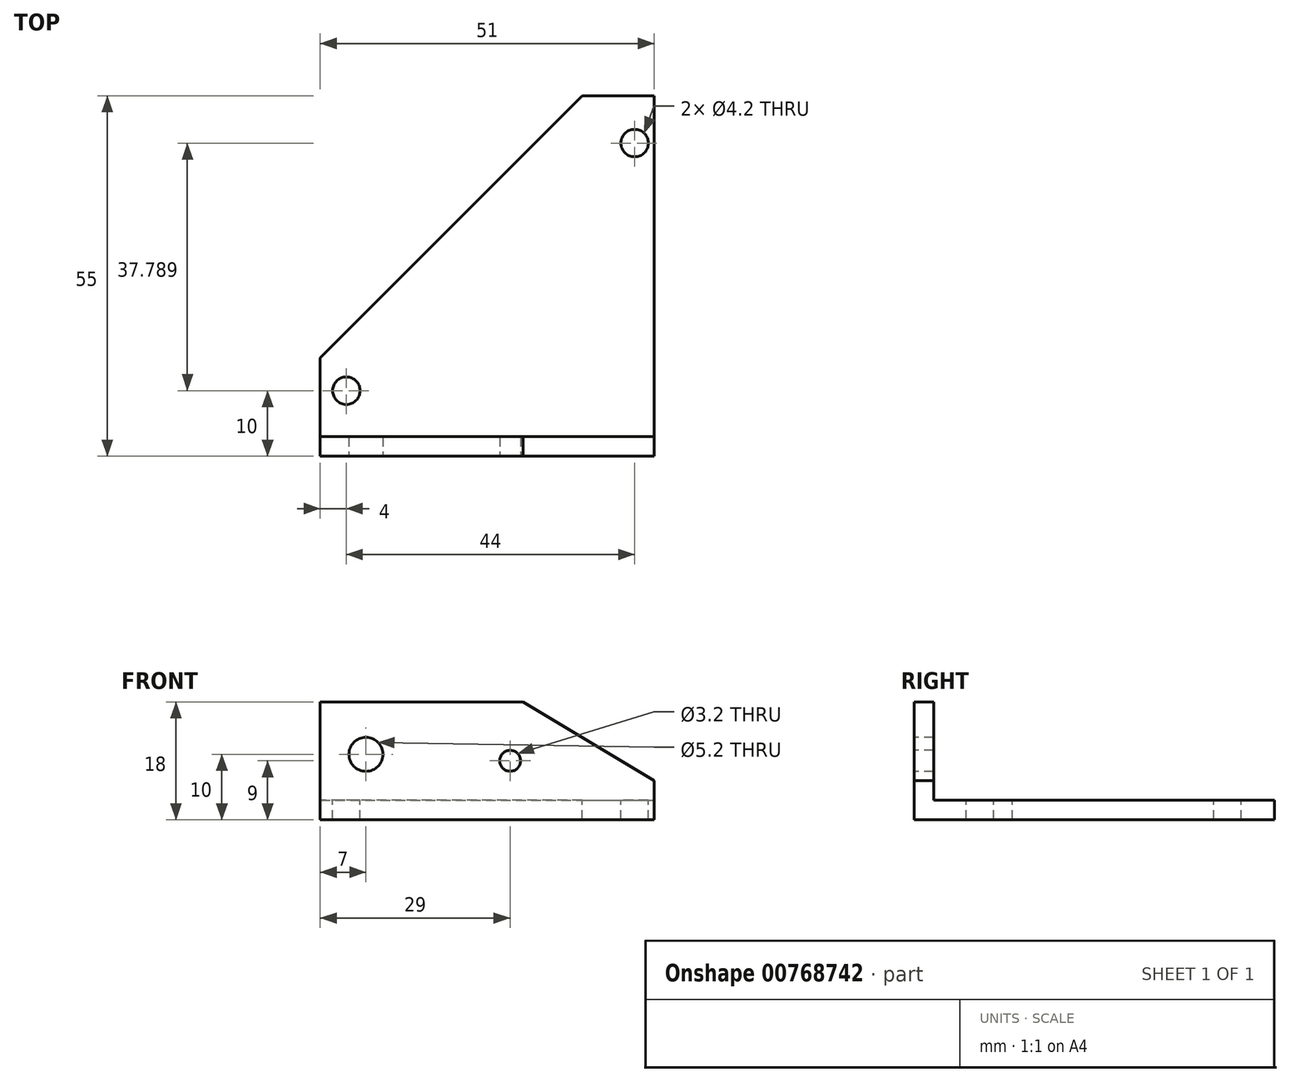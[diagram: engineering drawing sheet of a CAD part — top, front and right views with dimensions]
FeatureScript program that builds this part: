
annotation { "Feature Type Name" : "Feature", "Feature Type Description" : "" }
export const myFeature = defineFeature(function(context is Context, id is Id, definition is map)
    precondition{}
    {
        {
            var Q0;
            Q0=qCreatedBy(makeId("Top.planeOp"),FACE);
            var sketch = newSketch(context, id + "F0", { "sketchPlane" : qUnion([Q0])});
            skLineSegment(sketch, "E0.bottom", {"start": v(0, 0) * mm, "end": v(51, 0) * mm});
            skLineSegment(sketch, "E0.top", {"start": v(0, 55) * mm, "end": v(51, 55) * mm});
            skLineSegment(sketch, "E0.left", {"start": v(0, 0) * mm, "end": v(0, 55) * mm});
            skLineSegment(sketch, "E0.right", {"start": v(51, 0) * mm, "end": v(51, 55) * mm});
            skSolve(sketch);
        }
        {
            var Q0;
            Q0 = qSketchRegion(id + "F0", true);
            extrude(context, id + "F1", {"entities" : qUnion([Q0]), "depth" : 3 * mm, "offsetDistance" : 25 * mm});
        }
        {
            var Q0;
            Q0=makeQuery(id+"F1.opExtrude","CAP_FACE",FACE,{"disambiguationData":[OSD([sQuery(id+"F0.wireOp",EDGE,"E0.bottom"),sQuery(id+"F0.wireOp",EDGE,"E0.top"),sQuery(id+"F0.wireOp",EDGE,"E0.left"),sQuery(id+"F0.wireOp",EDGE,"E0.right")])],"isStart":false});
            var sketch = newSketch(context, id + "F2", { "sketchPlane" : qUnion([Q0])});
            skLineSegment(sketch, "E1.bottom", {"start": v(0, 0) * mm, "end": v(51, 0) * mm});
            skLineSegment(sketch, "E1.top", {"start": v(0, 3) * mm, "end": v(51, 3) * mm});
            skLineSegment(sketch, "E1.left", {"start": v(0, 0) * mm, "end": v(0, 3) * mm});
            skLineSegment(sketch, "E1.right", {"start": v(51, 0) * mm, "end": v(51, 3) * mm});
            skSolve(sketch);
        }
        {
            var Q0;
            Q0 = qSketchRegion(id + "F2", true);
            extrude(context, id + "F3", {"entities" : qUnion([Q0]), "operationType" : NewBodyOperationType.ADD, "depth" : 15 * mm, "offsetDistance" : 25 * mm});
        }
        {
            var Q0;
            Q0=makeQuery(id+"F3.boolean.opBoolean","MERGE",FACE,{"derivedFrom":[makeQuery(id+"F1.opExtrude","SWEPT_FACE",FACE,{"disambiguationData":[OSD([sQuery(id+"F0.wireOp",EDGE,"E0.bottom")])]}),makeQuery(id+"F3.opExtrude","SWEPT_FACE",FACE,{"disambiguationData":[OSD([sQuery(id+"F2.wireOp",EDGE,"E1.bottom")])]})]});
            var sketch = newSketch(context, id + "F4", { "sketchPlane" : qUnion([Q0])});
            skCircle(sketch, "E2", {"center": v(7, 10) * mm, "radius": 2.6 * mm});
            skCircle(sketch, "E3", {"center": v(29, 9) * mm, "radius": 1.6 * mm});
            skSolve(sketch);
        }
        {
            var Q0;
            Q0 = qSketchRegion(id + "F4", true);
            extrude(context, id + "F5", {"entities" : qUnion([Q0]), "operationType" : NewBodyOperationType.REMOVE, "oppositeDirection" : true, "depth" : 25 * mm, "offsetDistance" : 25 * mm});
        }
        {
            var Q0;
            Q0=makeQuery(id+"F1.opExtrude","CAP_FACE",FACE,{"disambiguationData":[OSD([sQuery(id+"F0.wireOp",EDGE,"E0.bottom"),sQuery(id+"F0.wireOp",EDGE,"E0.top"),sQuery(id+"F0.wireOp",EDGE,"E0.left"),sQuery(id+"F0.wireOp",EDGE,"E0.right")])],"isStart":false});
            var sketch = newSketch(context, id + "F6", { "sketchPlane" : qUnion([Q0])});
            skCircle(sketch, "E4", {"center": v(4, 10) * mm, "radius": 2.1 * mm});
            skCircle(sketch, "E5", {"center": v(48, 47.79) * mm, "radius": 2.1 * mm});
            skSolve(sketch);
        }
        {
            var Q0;
            Q0 = qSketchRegion(id + "F6", true);
            extrude(context, id + "F7", {"entities" : qUnion([Q0]), "operationType" : NewBodyOperationType.REMOVE, "oppositeDirection" : true, "depth" : 25 * mm, "offsetDistance" : 25 * mm});
        }
        {
            var Q0;
            Q0=makeQuery(id+"F1.opExtrude","CAP_FACE",FACE,{"disambiguationData":[OSD([sQuery(id+"F0.wireOp",EDGE,"E0.bottom"),sQuery(id+"F0.wireOp",EDGE,"E0.top"),sQuery(id+"F0.wireOp",EDGE,"E0.left"),sQuery(id+"F0.wireOp",EDGE,"E0.right")])],"isStart":false});
            var sketch = newSketch(context, id + "F8", { "sketchPlane" : qUnion([Q0])});
            skLineSegment(sketch, "E6", {"start": v(40, 55) * mm, "end": v(0, 15) * mm});
            skLineSegment(sketch, "E7", {"start": v(0, 15) * mm, "end": v(0, 55) * mm});
            skLineSegment(sketch, "E8", {"start": v(0, 55) * mm, "end": v(40, 55) * mm});
            skSolve(sketch);
        }
        {
            var Q0;
            Q0 = qSketchRegion(id + "F8", true);
            extrude(context, id + "F9", {"entities" : qUnion([Q0]), "operationType" : NewBodyOperationType.REMOVE, "oppositeDirection" : true, "depth" : 25 * mm, "offsetDistance" : 25 * mm});
        }
        {
            var Q0;
            Q0=makeQuery(id+"F3.opExtrude","SWEPT_FACE",FACE,{"disambiguationData":[OSD([sQuery(id+"F2.wireOp",EDGE,"E1.top")])]});
            var sketch = newSketch(context, id + "F10", { "sketchPlane" : qUnion([Q0])});
            skLineSegment(sketch, "E9", {"start": v(-31, 18) * mm, "end": v(-51, 6) * mm});
            skLineSegment(sketch, "E10", {"start": v(-51, 6) * mm, "end": v(-51, 18) * mm});
            skLineSegment(sketch, "E11", {"start": v(-51, 18) * mm, "end": v(-31, 18) * mm});
            skSolve(sketch);
        }
        {
            var Q0;
            Q0 = qSketchRegion(id + "F10", true);
            extrude(context, id + "F11", {"entities" : qUnion([Q0]), "operationType" : NewBodyOperationType.REMOVE, "oppositeDirection" : true, "depth" : 25 * mm, "offsetDistance" : 25 * mm});
        }
    });
